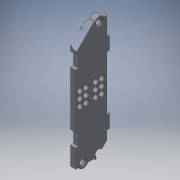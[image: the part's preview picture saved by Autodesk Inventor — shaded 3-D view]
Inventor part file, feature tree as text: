
AUTODESK INVENTOR PART (.ipt)
format: ipt  version: 2016 (Build 200138000, 138)  size: 313,856 bytes
history: native  units: in
note: dims shown in document units (in); Inventor stores cm internally (conversion verified against a paired STEP export)
features: reference x8, extrude x6, sketch x5, fillet x2, chamfer x1
ambient origin geometry x8: Origin, YZ Plane, XZ Plane, XY Plane, X Axis, Y Axis, Z Axis, Center Point
bodies: Solid1 (feature_tree)
feature tree (22):
  extrude  "Extrusion1"  Depth=1.1811in
  fillet  "Fillet1"  Radius=0.0787in
  extrude  "Extrusion3"  Depth=0.073in
  extrude  "Extrusion4"  Depth=0.7874in
  chamfer  "Chamfer1"  Distance=1.0in
  fillet  "Fillet2"  Radius=1.0in
  extrude  "Extrusion6"  Depth=0.0039in TaperAngle=45.0deg
  sketch  "Sketch7"  dims[d34=0.0118in d35=1.0in d36=0.0in d37=1.0in d38=0.0in d39=0.0197in d40=0.125in d41=45.0deg d42=0.0118in d47=0.002in d48=0.002in d49=1.0in d50=0.0in d51=0.0394in d52=0.0394in d53=0.1969in d54=0.0039in d55=1.0in d56=0.0in d57=1.0in d58=0.0in]
  extrude  "Extrusion7"  Depth=0.0118in
  extrude  "Extrusion8"  Depth=0.0039in
  sketch  "Sketch1"  dims[d0=0.0748in d1=1.1811in d3=0.1in d4=0.7874in d6=0.0902in]
  sketch  "Sketch3"  dims[d9=0.7874in d11=0.2362in d12=0.3937in d14=1.0in d16=0.0787in d17=0.0in]
  reference  "Reference1"
  reference  "Reference2"
  reference  "Reference3"
  reference  "Reference4"
  sketch  "Sketch4"  dims[d18=0.073in d19=0.073in]
  reference  "Reference5"
  reference  "Reference6"
  reference  "Reference7"
  reference  "Reference8"
  sketch  "Sketch6"  dims[d32=0.7874in d33=0.7874in]
